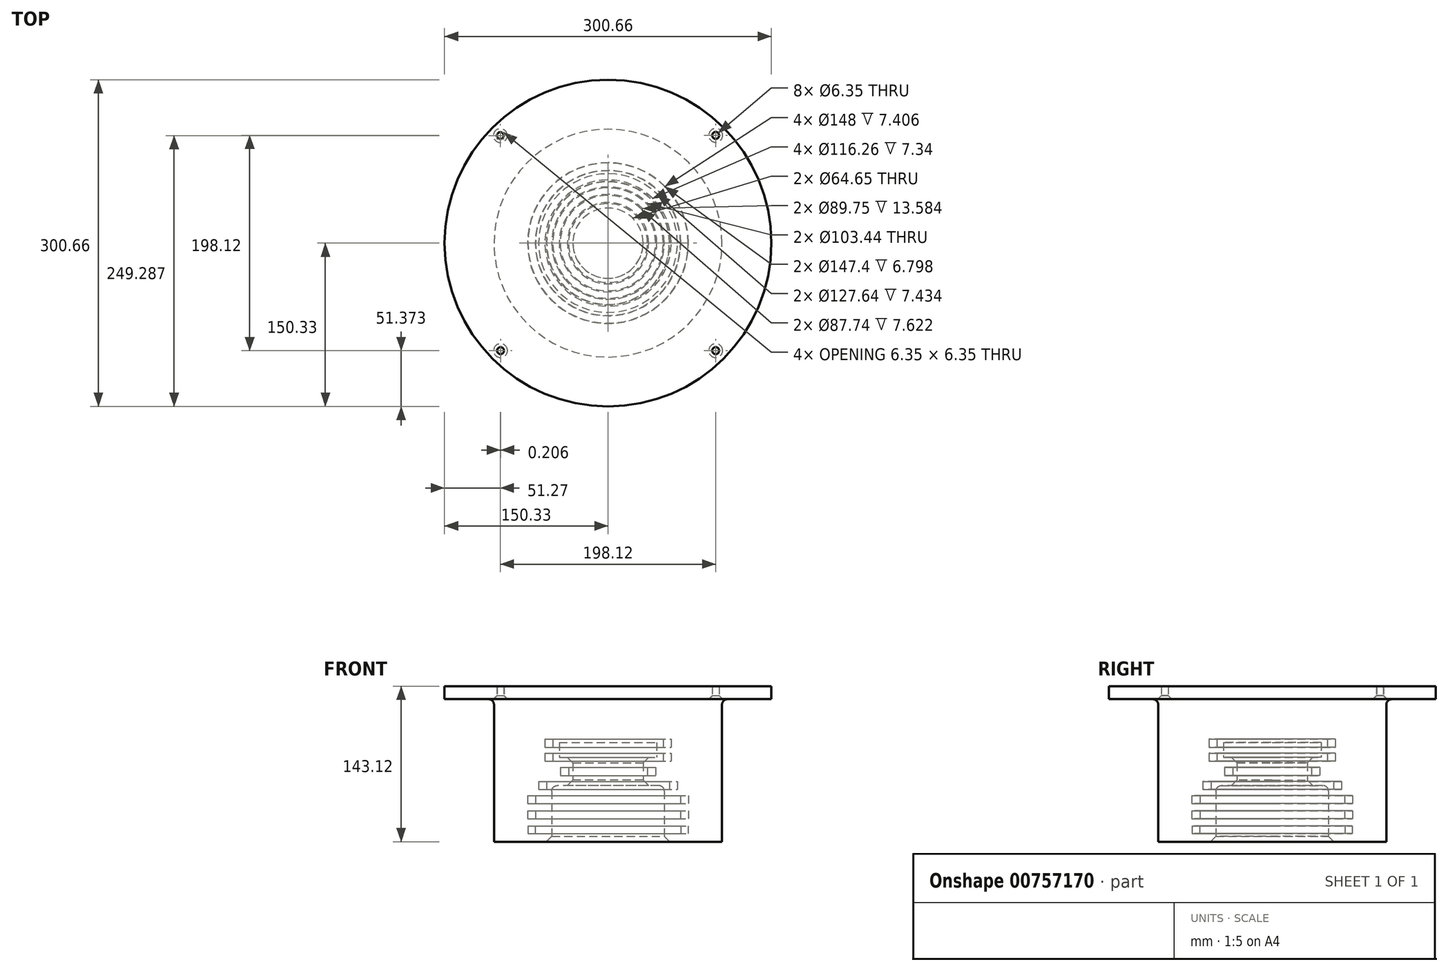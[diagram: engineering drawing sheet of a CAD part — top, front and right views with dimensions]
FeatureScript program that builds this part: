
annotation { "Feature Type Name" : "Feature", "Feature Type Description" : "" }
export const myFeature = defineFeature(function(context is Context, id is Id, definition is map)
    precondition{}
    {
        {
            var Q0;
            Q0=qCreatedBy(makeId("Front.planeOp"),FACE);
            var sketch = newSketch(context, id + "F0", { "sketchPlane" : qUnion([Q0])});
            skLineSegment(sketch, "E0", {"start": v(0, 0) * mm, "end": v(-51.72, 0) * mm, "construction": true});
            skLineSegment(sketch, "E1", {"start": v(-51.72, 0) * mm, "end": v(-51.72, 51.72) * mm});
            skLineSegment(sketch, "E2", {"start": v(-51.72, 51.72) * mm, "end": v(-32.32, 51.72) * mm});
            skLineSegment(sketch, "E3", {"start": v(-32.32, 51.72) * mm, "end": v(-32.32, 77.58) * mm});
            skLineSegment(sketch, "E4", {"start": v(-32.32, 77.58) * mm, "end": v(-44.88, 77.58) * mm});
            skLineSegment(sketch, "E5", {"start": v(-44.88, 77.58) * mm, "end": v(-44.88, 91.16) * mm});
            skLineSegment(sketch, "E6", {"start": v(-44.88, 91.16) * mm, "end": v(0, 91.16) * mm});
            skLineSegment(sketch, "E7", {"start": v(-51.72, 0) * mm, "end": v(-65.52, 0) * mm});
            skLineSegment(sketch, "E8", {"start": v(0, 131.18) * mm, "end": v(0, 91.16) * mm});
            skLineSegment(sketch, "E9", {"start": v(-104.89, 51.72) * mm, "end": v(-51.72, 51.72) * mm, "construction": true});
            skLineSegment(sketch, "E10", {"start": v(0, 143.12) * mm, "end": v(0, 91.16) * mm});
            skLineSegment(sketch, "E11", {"start": v(0, 10.93) * mm, "end": v(-66.9, 10.93) * mm, "construction": true});
            skLineSegment(sketch, "E12", {"start": v(0, 0) * mm, "end": v(0, 162.18) * mm, "construction": true});
            skLineSegment(sketch, "E13", {"start": v(0, 38.87) * mm, "end": v(-70.3, 38.87) * mm, "construction": true});
            skLineSegment(sketch, "E14", {"start": v(-70.3, 38.87) * mm, "end": v(-70.3, 97.78) * mm, "construction": true});
            skLineSegment(sketch, "E15", {"start": v(-70.3, 51.83) * mm, "end": v(0, 51.83) * mm, "construction": true});
            skLineSegment(sketch, "E16", {"start": v(0, 64.79) * mm, "end": v(-70.3, 64.79) * mm, "construction": true});
            skLineSegment(sketch, "E17", {"start": v(-70.3, 77.74) * mm, "end": v(0, 77.74) * mm, "construction": true});
            skLineSegment(sketch, "E18", {"start": v(-70.3, 90.7) * mm, "end": v(0, 90.7) * mm, "construction": true});
            skLineSegment(sketch, "E19", {"start": v(-104.89, 131.18) * mm, "end": v(-150.33, 131.18) * mm});
            skLineSegment(sketch, "E20", {"start": v(-150.33, 131.18) * mm, "end": v(-150.33, 143.12) * mm});
            skLineSegment(sketch, "E21", {"start": v(-150.33, 143.12) * mm, "end": v(0, 143.12) * mm});
            skLineSegment(sketch, "E22", {"start": v(-104.89, 131.18) * mm, "end": v(-104.89, 0) * mm});
            skLineSegment(sketch, "E23", {"start": v(-65.52, 0) * mm, "end": v(-104.89, 0) * mm});
            skLineSegment(sketch, "E24", {"start": v(-66.9, 10.93) * mm, "end": v(-165.47, 10.93) * mm, "construction": true});
            skLineSegment(sketch, "E25", {"start": v(-70.3, 38.87) * mm, "end": v(-172.32, 38.87) * mm, "construction": true});
            skLineSegment(sketch, "E26.bottom", {"start": v(-66.9, 7.53) * mm, "end": v(-73.7, 7.53) * mm});
            skLineSegment(sketch, "E26.top", {"start": v(-66.9, 14.33) * mm, "end": v(-73.7, 14.33) * mm});
            skLineSegment(sketch, "E26.left", {"start": v(-66.9, 7.53) * mm, "end": v(-66.9, 14.33) * mm});
            skLineSegment(sketch, "E26.right", {"start": v(-73.7, 7.53) * mm, "end": v(-73.7, 14.33) * mm});
            skPoint(sketch, "E26.middle", {"position": v(-70.3, 10.93) * mm});
            skLineSegment(sketch, "E27", {"start": v(0, 24.9) * mm, "end": v(-124.94, 24.9) * mm, "construction": true});
            skLineSegment(sketch, "E28.bottom", {"start": v(-66.6, 21.2) * mm, "end": v(-74, 21.2) * mm});
            skLineSegment(sketch, "E28.top", {"start": v(-66.6, 28.6) * mm, "end": v(-74, 28.6) * mm});
            skLineSegment(sketch, "E28.left", {"start": v(-66.6, 21.2) * mm, "end": v(-66.6, 28.6) * mm});
            skLineSegment(sketch, "E28.right", {"start": v(-74, 21.2) * mm, "end": v(-74, 28.6) * mm});
            skPoint(sketch, "E28.middle", {"position": v(-70.3, 24.9) * mm});
            skPoint(sketch, "E28.middle.positionSnap0", {"position": v(-70.3, 14.33) * mm});
            skPoint(sketch, "E28.centerSnap0", {"position": v(-70.3, 14.33) * mm});
            skLineSegment(sketch, "E29.bottom", {"start": v(-66.6, 35.17) * mm, "end": v(-74, 35.17) * mm});
            skLineSegment(sketch, "E29.top", {"start": v(-66.6, 42.57) * mm, "end": v(-74, 42.57) * mm});
            skLineSegment(sketch, "E29.left", {"start": v(-66.6, 35.17) * mm, "end": v(-66.6, 42.57) * mm});
            skLineSegment(sketch, "E29.right", {"start": v(-74, 35.17) * mm, "end": v(-74, 42.57) * mm});
            skPoint(sketch, "E29.middle", {"position": v(-70.3, 38.87) * mm});
            skLineSegment(sketch, "E30.bottom", {"start": v(-56.39, 48.11) * mm, "end": v(-63.82, 48.11) * mm});
            skLineSegment(sketch, "E30.top", {"start": v(-56.39, 55.55) * mm, "end": v(-63.82, 55.55) * mm});
            skLineSegment(sketch, "E30.left", {"start": v(-56.39, 48.11) * mm, "end": v(-56.39, 55.55) * mm});
            skLineSegment(sketch, "E30.right", {"start": v(-63.82, 48.11) * mm, "end": v(-63.82, 55.55) * mm});
            skPoint(sketch, "E30.middle", {"position": v(-60.1, 51.83) * mm});
            skLineSegment(sketch, "E31.bottom", {"start": v(-36.25, 60.97) * mm, "end": v(-43.87, 60.97) * mm});
            skLineSegment(sketch, "E31.top", {"start": v(-36.25, 68.6) * mm, "end": v(-43.87, 68.6) * mm});
            skLineSegment(sketch, "E31.left", {"start": v(-36.25, 60.97) * mm, "end": v(-36.25, 68.6) * mm});
            skLineSegment(sketch, "E31.right", {"start": v(-43.87, 60.97) * mm, "end": v(-43.87, 68.6) * mm});
            skPoint(sketch, "E31.middle", {"position": v(-40.06, 64.79) * mm});
            skLineSegment(sketch, "E32.bottom", {"start": v(-50.79, 74.07) * mm, "end": v(-58.13, 74.07) * mm});
            skLineSegment(sketch, "E32.top", {"start": v(-50.79, 81.41) * mm, "end": v(-58.13, 81.41) * mm});
            skLineSegment(sketch, "E32.left", {"start": v(-50.79, 74.07) * mm, "end": v(-50.79, 81.41) * mm});
            skLineSegment(sketch, "E32.right", {"start": v(-58.13, 74.07) * mm, "end": v(-58.13, 81.41) * mm});
            skPoint(sketch, "E32.middle", {"position": v(-54.46, 77.74) * mm});
            skLineSegment(sketch, "E33.bottom", {"start": v(-50.79, 87.03) * mm, "end": v(-58.13, 87.03) * mm});
            skLineSegment(sketch, "E33.top", {"start": v(-50.79, 94.37) * mm, "end": v(-58.13, 94.37) * mm});
            skLineSegment(sketch, "E33.left", {"start": v(-50.79, 87.03) * mm, "end": v(-50.79, 94.37) * mm});
            skLineSegment(sketch, "E33.right", {"start": v(-58.13, 87.03) * mm, "end": v(-58.13, 94.37) * mm});
            skPoint(sketch, "E33.middle", {"position": v(-54.46, 90.7) * mm});
            skPoint(sketch, "E33.middle.positionSnap0", {"position": v(-54.46, 81.41) * mm});
            skPoint(sketch, "E33.centerSnap0", {"position": v(-54.46, 81.41) * mm});
            skSolve(sketch);
        }
        {
            var Q0;
            Q0=makeQuery(id+"F0.imprint","IMPRINT",FACE,{"disambiguationData":[TD([[makeQuery(id+"F0.imprint","IMPRINT",EDGE,{"derivedFrom":sQuery(id+"F0.wireOp",EDGE,"E1")}),1.0]])]});
            var Q1;
            Q1=sQuery(id+"F0.wireOp",EDGE,"E12");
            revolve(context, id + "F1", {"surfaceOperationType" : NewSurfaceOperationType.NEW, "entities" : qUnion([Q0]), "axis" : qUnion([Q1]), "revolveType" : RevolveType.ONE_DIRECTION, "angle" : 360 * degree});
        }
        {
            var Q0;
            Q0=makeQuery(id+"F1.opRevolve","SWEPT_EDGE",EDGE,{"disambiguationData":[OSD([sQuery(id+"F0.wireOp",EDGE,"E1"),sQuery(id+"F0.wireOp",EDGE,"E7")])]});
            chamfer(context, id + "F2", {"entities" : qUnion([Q0]), "width" : 5.08 * mm, "tangentPropagation" : true});
        }
        {
            var Q0;
            Q0=makeQuery(id+"F1.opRevolve","SWEPT_EDGE",EDGE,{"disambiguationData":[OSD([sQuery(id+"F0.wireOp",EDGE,"E2"),sQuery(id+"F0.wireOp",EDGE,"E3")])]});
            var Q1;
            Q1=makeQuery(id+"F1.opRevolve","SWEPT_EDGE",EDGE,{"disambiguationData":[OSD([sQuery(id+"F0.wireOp",EDGE,"E3"),sQuery(id+"F0.wireOp",EDGE,"E4")])]});
            chamfer(context, id + "F3", {"entities" : qUnion([Q0, Q1]), "width" : 5.08 * mm, "tangentPropagation" : true});
        }
        {
            var Q0;
            Q0=makeQuery(id+"F1.opRevolve","SWEPT_EDGE",EDGE,{"disambiguationData":[OSD([sQuery(id+"F0.wireOp",EDGE,"E1"),sQuery(id+"F0.wireOp",EDGE,"E2")])]});
            fillet(context, id + "F4", {"entities" : qUnion([Q0]), "radius" : 5.08 * mm, "tangentPropagation" : true, "allowEdgeOverflow" : false});
        }
        {
            var Q0;
            Q0=makeQuery(id+"F1.opRevolve","SWEPT_FACE",FACE,{"disambiguationData":[OSD([sQuery(id+"F0.wireOp",EDGE,"E19")])]});
            cPlane(context, id + "F5", {"entities" : qUnion([Q0]), "cplaneType" : CPlaneType.OFFSET, "offset" : 0 * mm, "width" : 152.4 * mm, "height" : 152.4 * mm});
        }
        {
            var Q0;
            Q0=qCreatedBy(id+"F5.planeOp",FACE);
            var sketch = newSketch(context, id + "F6", { "sketchPlane" : qUnion([Q0])});
            skLineSegment(sketch, "E34", {"start": v(0, 0) * mm, "end": v(0, 202.26) * mm, "construction": true});
            skLineSegment(sketch, "E35", {"start": v(0, 202.26) * mm, "end": v(0, -245.4) * mm, "construction": true});
            skPoint(sketch, "E35.endSnap0", {"position": v(0, 101.13) * mm});
            skLineSegment(sketch, "E36", {"start": v(0, 0) * mm, "end": v(161.7, 0) * mm, "construction": true});
            skLineSegment(sketch, "E37", {"start": v(161.7, 161.53) * mm, "end": v(0, 0) * mm, "construction": true});
            skLineSegment(sketch, "E38", {"start": v(0, 0) * mm, "end": v(132.47, -132.6) * mm, "construction": true});
            skLineSegment(sketch, "E39", {"start": v(132.47, -132.6) * mm, "end": v(-149.53, 149.68) * mm, "construction": true});
            skLineSegment(sketch, "E40", {"start": v(99.06, 98.96) * mm, "end": v(99.06, -160.87) * mm, "construction": true});
            skLineSegment(sketch, "E41", {"start": v(-99.06, 176.87) * mm, "end": v(-99.06, -197.26) * mm, "construction": true});
            skPoint(sketch, "E42", {"position": v(99.06, -99.16) * mm});
            skPoint(sketch, "E43", {"position": v(-98.85, 98.96) * mm});
            skLineSegment(sketch, "E44", {"start": v(0, 0) * mm, "end": v(-153.41, -153.25) * mm, "construction": true});
            skPoint(sketch, "E45", {"position": v(-99.06, -98.96) * mm});
            skSolve(sketch);
        }
        {
            var Q0;
            Q0=sQuery(id+"F6.wireOp",VERTEX,"E43");
            var Q1;
            Q1=sQuery(id+"F6.wireOp",VERTEX,"E40.start");
            var Q2;
            Q2=sQuery(id+"F6.wireOp",VERTEX,"E42");
            var Q3;
            Q3=sQuery(id+"F6.wireOp",VERTEX,"E45");
            var Q4;
            Q4=makeQuery(id+"F1.opRevolve","SWEPT_BODY",BODY,{"disambiguationData":[OSD([sQuery(id+"F0.wireOp",EDGE,"E1"),sQuery(id+"F0.wireOp",EDGE,"E2"),sQuery(id+"F0.wireOp",EDGE,"E3"),sQuery(id+"F0.wireOp",EDGE,"E4"),sQuery(id+"F0.wireOp",EDGE,"E5"),sQuery(id+"F0.wireOp",EDGE,"E6"),sQuery(id+"F0.wireOp",EDGE,"E7"),sQuery(id+"F0.wireOp",EDGE,"E10"),sQuery(id+"F0.wireOp",EDGE,"E19"),sQuery(id+"F0.wireOp",EDGE,"E20"),sQuery(id+"F0.wireOp",EDGE,"E21"),sQuery(id+"F0.wireOp",EDGE,"E22"),sQuery(id+"F0.wireOp",EDGE,"E23")])]});
            hole(context, id + "F7", {"style" : HoleStyle.C_SINK, "endStyle" : HoleEndStyle.THROUGH, "holeDiameter" : 6.35 * mm, "cSinkDiameter" : 12.7 * mm, "cSinkAngle" : 90 * degree, "majorDiameter" : 6.35 * mm, "isTappedThrough" : true, "tappedDepth" : 12.7 * mm, "tapClearance" : 3, "locations" : qUnion([Q0, Q1, Q2, Q3]), "scope" : qUnion([Q4])});
        }
        {
            var Q0;
            Q0=makeQuery(id+"F1.opRevolve","SWEPT_EDGE",EDGE,{"disambiguationData":[OSD([sQuery(id+"F0.wireOp",EDGE,"E19"),sQuery(id+"F0.wireOp",EDGE,"E22")])]});
            fillet(context, id + "F8", {"entities" : qUnion([Q0]), "radius" : 5.08 * mm, "tangentPropagation" : true, "allowEdgeOverflow" : false});
        }
    });
